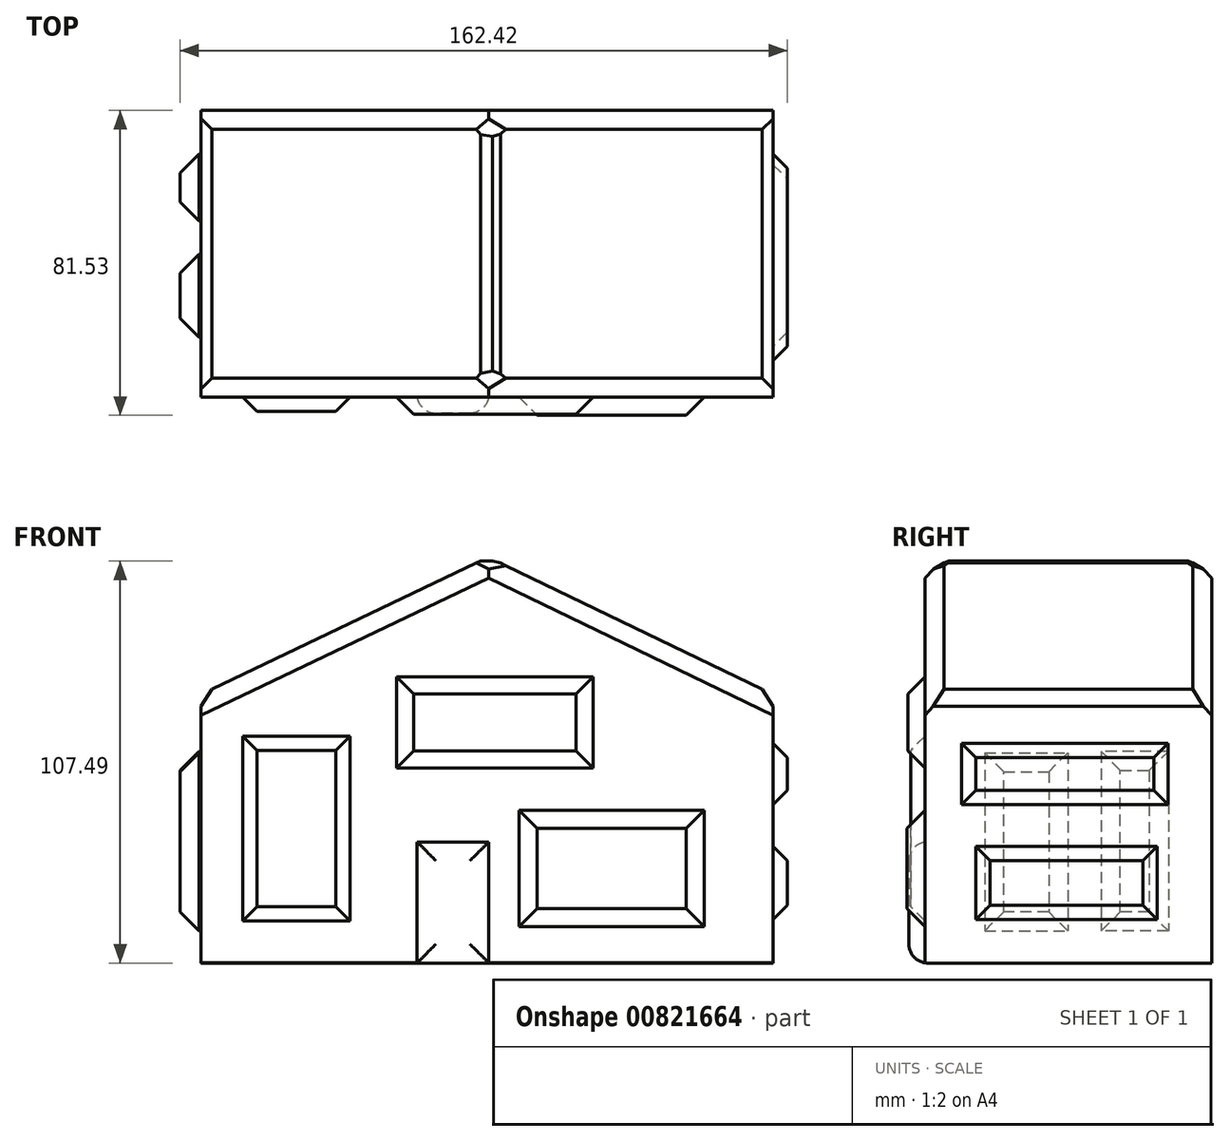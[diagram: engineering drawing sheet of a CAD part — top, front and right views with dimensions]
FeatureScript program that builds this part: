
annotation { "Feature Type Name" : "Feature", "Feature Type Description" : "" }
export const myFeature = defineFeature(function(context is Context, id is Id, definition is map)
    precondition{}
    {
        {
            var Q0;
            Q0=qCreatedBy(makeId("Front.planeOp"),FACE);
            var sketch = newSketch(context, id + "F0", { "sketchPlane" : qUnion([Q0])});
            skLineSegment(sketch, "E0.bottom", {"start": v(-76.96, 30.78) * mm, "end": v(76.06, 30.78) * mm});
            skLineSegment(sketch, "E0.top", {"start": v(-76.96, -41.12) * mm, "end": v(76.06, -41.12) * mm});
            skLineSegment(sketch, "E0.left", {"start": v(-76.96, 30.78) * mm, "end": v(-76.96, -41.12) * mm});
            skLineSegment(sketch, "E0.right", {"start": v(76.06, 30.78) * mm, "end": v(76.06, -41.12) * mm});
            skLineSegment(sketch, "E1", {"start": v(-76.96, 30.78) * mm, "end": v(0, 67.42) * mm});
            skLineSegment(sketch, "E2", {"start": v(0, 67.42) * mm, "end": v(76.06, 30.78) * mm});
            skLineSegment(sketch, "E3.bottom", {"start": v(-67.03, 20.84) * mm, "end": v(-35.77, 20.84) * mm});
            skLineSegment(sketch, "E3.top", {"start": v(-67.03, -31.09) * mm, "end": v(-35.77, -31.09) * mm});
            skLineSegment(sketch, "E3.left", {"start": v(-67.03, 20.84) * mm, "end": v(-67.03, -31.09) * mm});
            skLineSegment(sketch, "E3.right", {"start": v(-35.77, 20.84) * mm, "end": v(-35.77, -31.09) * mm});
            skLineSegment(sketch, "E4.bottom", {"start": v(-19.13, -41.12) * mm, "end": v(0, -41.12) * mm});
            skLineSegment(sketch, "E4.top", {"start": v(-19.13, -8.76) * mm, "end": v(0, -8.76) * mm});
            skLineSegment(sketch, "E4.left", {"start": v(-19.13, -41.12) * mm, "end": v(-19.13, -8.76) * mm});
            skLineSegment(sketch, "E4.right", {"start": v(0, -41.12) * mm, "end": v(0, -8.76) * mm});
            skLineSegment(sketch, "E5.bottom", {"start": v(-25.13, 35.93) * mm, "end": v(28.47, 35.93) * mm});
            skLineSegment(sketch, "E5.top", {"start": v(-25.13, 10.5) * mm, "end": v(28.47, 10.5) * mm});
            skLineSegment(sketch, "E5.left", {"start": v(-25.13, 35.93) * mm, "end": v(-25.13, 10.5) * mm});
            skLineSegment(sketch, "E5.right", {"start": v(28.47, 35.93) * mm, "end": v(28.47, 10.5) * mm});
            skLineSegment(sketch, "E6.bottom", {"start": v(57.96, 0) * mm, "end": v(7.9, 0) * mm});
            skLineSegment(sketch, "E6.top", {"start": v(57.96, -31.61) * mm, "end": v(7.9, -31.61) * mm});
            skLineSegment(sketch, "E6.left", {"start": v(57.96, 0) * mm, "end": v(57.96, -31.61) * mm});
            skLineSegment(sketch, "E6.right", {"start": v(7.9, 0) * mm, "end": v(7.9, -31.61) * mm});
            skSolve(sketch);
        }
        {
            var Q0;
            {var subQ1=sQuery(id+"F0.wireOp",EDGE,"E0.left");Q0=makeQuery(id+"F0.imprint","IMPRINT",FACE,{"disambiguationData":[TD([[makeQuery(id+"F0.imprint","IMPRINT",EDGE,{"derivedFrom":subQ1}),1.0]])]});}
            extrude(context, id + "F1", {"entities" : qUnion([Q0]), "depth" : 75.95 * mm, "offsetDistance" : 25.4 * mm});
        }
        {
            var Q0;
            {var subQ5=sQuery(id+"F0.wireOp",EDGE,"E1");Q0=makeQuery(id+"F0.imprint","IMPRINT",FACE,{"disambiguationData":[TD([[makeQuery(id+"F0.imprint","IMPRINT",EDGE,{"derivedFrom":subQ5}),-1.0]])]});}
            var Q1;
            {var subQ1=sQuery(id+"F0.wireOp",EDGE,"E0.left");Q1=makeQuery(id+"F0.imprint","IMPRINT",FACE,{"disambiguationData":[TD([[makeQuery(id+"F0.imprint","IMPRINT",EDGE,{"derivedFrom":subQ1}),1.0]])]});}
            extrude(context, id + "F2", {"entities" : qUnion([Q0, Q1]), "operationType" : NewBodyOperationType.ADD, "depth" : 76.7 * mm, "offsetDistance" : 25.4 * mm});
        }
        {
            var Q0;
            Q0=makeQuery(id+"F0.imprint","IMPRINT",FACE,{"disambiguationData":[TD([[makeQuery(id+"F0.imprint","IMPRINT",EDGE,{"derivedFrom":sQuery(id+"F0.wireOp",EDGE,"E3.bottom")}),-1.0]])]});
            extrude(context, id + "F3", {"entities" : qUnion([Q0]), "operationType" : NewBodyOperationType.ADD, "depth" : 80.52 * mm, "offsetDistance" : 25.4 * mm});
        }
        {
            var Q0;
            Q0=makeQuery(id+"F2.opExtrude","SWEPT_FACE",FACE,{"disambiguationData":[OSD([sQuery(id+"F0.wireOp",EDGE,"E1")])]});
            chamfer(context, id + "F4", {"entities" : qUnion([Q0]), "width" : 5.08 * mm, "tangentPropagation" : true});
        }
        {
            var Q0;
            Q0=makeQuery(id+"F2.opExtrude","SWEPT_FACE",FACE,{"disambiguationData":[OSD([sQuery(id+"F0.wireOp",EDGE,"E2")])]});
            chamfer(context, id + "F5", {"entities" : qUnion([Q0]), "width" : 5.08 * mm, "tangentPropagation" : true});
        }
        {
            var Q0;
            Q0=makeQuery(id+"F3.opExtrude","CAP_FACE",FACE,{"disambiguationData":[OSD([sQuery(id+"F0.wireOp",EDGE,"E3.bottom"),sQuery(id+"F0.wireOp",EDGE,"E3.top"),sQuery(id+"F0.wireOp",EDGE,"E3.left"),sQuery(id+"F0.wireOp",EDGE,"E3.right")])],"isStart":false});
            chamfer(context, id + "F6", {"entities" : qUnion([Q0]), "width" : 5.08 * mm, "tangentPropagation" : true});
        }
        {
            var Q0;
            Q0=makeQuery(id+"F0.imprint","IMPRINT",FACE,{"disambiguationData":[TD([[makeQuery(id+"F0.imprint","IMPRINT",EDGE,{"derivedFrom":sQuery(id+"F0.wireOp",EDGE,"E4.top")}),-1.0]])]});
            extrude(context, id + "F7", {"entities" : qUnion([Q0]), "operationType" : NewBodyOperationType.ADD, "depth" : 81.03 * mm, "offsetDistance" : 25.4 * mm});
        }
        {
            var Q0;
            Q0=makeQuery(id+"F7.opExtrude","CAP_FACE",FACE,{"disambiguationData":[OSD([sQuery(id+"F0.wireOp",EDGE,"E0.top"),sQuery(id+"F0.wireOp",EDGE,"E4.top"),sQuery(id+"F0.wireOp",EDGE,"E4.left"),sQuery(id+"F0.wireOp",EDGE,"E4.right")])],"isStart":false});
            fillet(context, id + "F8", {"entities" : qUnion([Q0]), "radius" : 5.08 * mm, "tangentPropagation" : true, "allowEdgeOverflow" : false});
        }
        {
            var Q0;
            {var subQ5=sQuery(id+"F0.wireOp",EDGE,"E5.top");Q0=makeQuery(id+"F0.imprint","IMPRINT",FACE,{"disambiguationData":[TD([[makeQuery(id+"F0.imprint","IMPRINT",EDGE,{"derivedFrom":subQ5}),1.0]])]});}
            var Q1;
            {var subQ5=sQuery(id+"F0.wireOp",EDGE,"E5.bottom");Q1=makeQuery(id+"F0.imprint","IMPRINT",FACE,{"disambiguationData":[TD([[makeQuery(id+"F0.imprint","IMPRINT",EDGE,{"derivedFrom":subQ5}),-1.0]])]});}
            extrude(context, id + "F9", {"entities" : qUnion([Q0, Q1]), "operationType" : NewBodyOperationType.ADD, "depth" : 81.28 * mm, "offsetDistance" : 25.4 * mm});
        }
        {
            var Q0;
            Q0=makeQuery(id+"F9.opExtrude","CAP_FACE",FACE,{"disambiguationData":[OSD([sQuery(id+"F0.wireOp",EDGE,"E5.bottom"),sQuery(id+"F0.wireOp",EDGE,"E5.top"),sQuery(id+"F0.wireOp",EDGE,"E5.left"),sQuery(id+"F0.wireOp",EDGE,"E5.right")])],"isStart":false});
            chamfer(context, id + "F10", {"entities" : qUnion([Q0]), "width" : 5.08 * mm, "tangentPropagation" : true});
        }
        {
            var Q0;
            Q0=makeQuery(id+"F0.imprint","IMPRINT",FACE,{"disambiguationData":[TD([[makeQuery(id+"F0.imprint","IMPRINT",EDGE,{"derivedFrom":sQuery(id+"F0.wireOp",EDGE,"E6.bottom")}),1.0]])]});
            extrude(context, id + "F11", {"entities" : qUnion([Q0]), "operationType" : NewBodyOperationType.ADD, "depth" : 81.53 * mm, "offsetDistance" : 25.4 * mm});
        }
        {
            var Q0;
            Q0=makeQuery(id+"F11.opExtrude","CAP_FACE",FACE,{"disambiguationData":[OSD([sQuery(id+"F0.wireOp",EDGE,"E6.bottom"),sQuery(id+"F0.wireOp",EDGE,"E6.top"),sQuery(id+"F0.wireOp",EDGE,"E6.left"),sQuery(id+"F0.wireOp",EDGE,"E6.right")])],"isStart":false});
            chamfer(context, id + "F12", {"entities" : qUnion([Q0]), "width" : 5.08 * mm, "tangentPropagation" : true});
        }
        {
            var Q0;
            {var subQ0=sQuery(id+"F0.wireOp",EDGE,"E0.right");Q0=makeQuery(id+"F2.boolean.opBoolean","MERGE",FACE,{"derivedFrom":[makeQuery(id+"F1.opExtrude","SWEPT_FACE",FACE,{"disambiguationData":[OSD([subQ0])]}),makeQuery(id+"F2.opExtrude","SWEPT_FACE",FACE,{"disambiguationData":[OSD([subQ0])]})]});}
            var sketch = newSketch(context, id + "F13", { "sketchPlane" : qUnion([Q0])});
            skLineSegment(sketch, "E7.bottom", {"start": v(-64.4, -30.71) * mm, "end": v(-13.26, -30.71) * mm});
            skLineSegment(sketch, "E7.top", {"start": v(-64.4, -8.7) * mm, "end": v(-13.26, -8.7) * mm});
            skLineSegment(sketch, "E7.left", {"start": v(-64.4, -30.71) * mm, "end": v(-64.4, -8.7) * mm});
            skLineSegment(sketch, "E7.right", {"start": v(-13.26, -30.71) * mm, "end": v(-13.26, -8.7) * mm});
            skLineSegment(sketch, "E8.bottom", {"start": v(-68.21, 18.96) * mm, "end": v(-10.34, 18.96) * mm});
            skLineSegment(sketch, "E8.top", {"start": v(-68.21, 0) * mm, "end": v(-10.34, 0) * mm});
            skLineSegment(sketch, "E8.left", {"start": v(-68.21, 18.96) * mm, "end": v(-68.21, 0) * mm});
            skLineSegment(sketch, "E8.right", {"start": v(-10.34, 18.96) * mm, "end": v(-10.34, 0) * mm});
            skSolve(sketch);
        }
        {
            var Q0;
            Q0=makeQuery(id+"F13.imprint","IMPRINT",FACE,{"disambiguationData":[TD([[makeQuery(id+"F13.imprint","IMPRINT",EDGE,{"derivedFrom":sQuery(id+"F13.wireOp",EDGE,"E7.bottom")}),1.0]])]});
            var Q1;
            Q1=makeQuery(id+"F13.imprint","IMPRINT",FACE,{"disambiguationData":[TD([[makeQuery(id+"F13.imprint","IMPRINT",EDGE,{"derivedFrom":sQuery(id+"F13.wireOp",EDGE,"E8.bottom")}),-1.0]])]});
            extrude(context, id + "F14", {"entities" : qUnion([Q0, Q1]), "operationType" : NewBodyOperationType.ADD, "depth" : 3.8 * mm, "offsetDistance" : 25.4 * mm});
        }
        {
            var Q0;
            Q0=makeQuery(id+"F14.opExtrude","CAP_FACE",FACE,{"disambiguationData":[OSD([sQuery(id+"F13.wireOp",EDGE,"E8.bottom"),sQuery(id+"F13.wireOp",EDGE,"E8.top"),sQuery(id+"F13.wireOp",EDGE,"E8.left"),sQuery(id+"F13.wireOp",EDGE,"E8.right")])],"isStart":false});
            var Q1;
            Q1=makeQuery(id+"F14.opExtrude","CAP_EDGE",EDGE,{"disambiguationData":[OSD([sQuery(id+"F13.wireOp",EDGE,"E7.right")])],"isStart":false});
            var Q2;
            Q2=makeQuery(id+"F14.opExtrude","CAP_FACE",FACE,{"disambiguationData":[OSD([sQuery(id+"F13.wireOp",EDGE,"E7.bottom"),sQuery(id+"F13.wireOp",EDGE,"E7.top"),sQuery(id+"F13.wireOp",EDGE,"E7.left"),sQuery(id+"F13.wireOp",EDGE,"E7.right")])],"isStart":false});
            chamfer(context, id + "F15", {"entities" : qUnion([Q0, Q1, Q2]), "width" : 5.08 * mm, "tangentPropagation" : true});
        }
        {
            var Q0;
            {var subQ0=sQuery(id+"F0.wireOp",EDGE,"E0.left");Q0=makeQuery(id+"F2.boolean.opBoolean","MERGE",FACE,{"derivedFrom":[makeQuery(id+"F1.opExtrude","SWEPT_FACE",FACE,{"disambiguationData":[OSD([subQ0])]}),makeQuery(id+"F2.opExtrude","SWEPT_FACE",FACE,{"disambiguationData":[OSD([subQ0])]})]});}
            var sketch = newSketch(context, id + "F16", { "sketchPlane" : qUnion([Q0])});
            skLineSegment(sketch, "E9.bottom", {"start": v(11.6, 15.46) * mm, "end": v(29.56, 15.46) * mm});
            skLineSegment(sketch, "E9.top", {"start": v(11.6, -32.55) * mm, "end": v(29.56, -32.55) * mm});
            skLineSegment(sketch, "E9.left", {"start": v(11.6, 15.46) * mm, "end": v(11.6, -32.55) * mm});
            skLineSegment(sketch, "E9.right", {"start": v(29.56, 15.46) * mm, "end": v(29.56, -32.55) * mm});
            skLineSegment(sketch, "E10.bottom", {"start": v(60.74, 15.15) * mm, "end": v(38.5, 15.15) * mm});
            skLineSegment(sketch, "E10.top", {"start": v(60.74, -32.55) * mm, "end": v(38.5, -32.55) * mm});
            skLineSegment(sketch, "E10.left", {"start": v(60.74, 15.15) * mm, "end": v(60.74, -32.55) * mm});
            skLineSegment(sketch, "E10.right", {"start": v(38.5, 15.15) * mm, "end": v(38.5, -32.55) * mm});
            skSolve(sketch);
        }
        {
            var Q0;
            Q0 = qSketchRegion(id + "F16", true);
            extrude(context, id + "F17", {"entities" : qUnion([Q0]), "operationType" : NewBodyOperationType.ADD, "depth" : 5.6 * mm, "offsetDistance" : 25.4 * mm});
        }
        {
            var Q0;
            Q0=makeQuery(id+"F17.opExtrude","CAP_FACE",FACE,{"disambiguationData":[OSD([sQuery(id+"F16.wireOp",EDGE,"E10.bottom"),sQuery(id+"F16.wireOp",EDGE,"E10.top"),sQuery(id+"F16.wireOp",EDGE,"E10.left"),sQuery(id+"F16.wireOp",EDGE,"E10.right")])],"isStart":false});
            var Q1;
            Q1=makeQuery(id+"F17.opExtrude","CAP_FACE",FACE,{"disambiguationData":[OSD([sQuery(id+"F16.wireOp",EDGE,"E9.bottom"),sQuery(id+"F16.wireOp",EDGE,"E9.top"),sQuery(id+"F16.wireOp",EDGE,"E9.left"),sQuery(id+"F16.wireOp",EDGE,"E9.right")])],"isStart":false});
            chamfer(context, id + "F18", {"entities" : qUnion([Q0, Q1]), "width" : 5.08 * mm, "tangentPropagation" : true});
        }
    });
